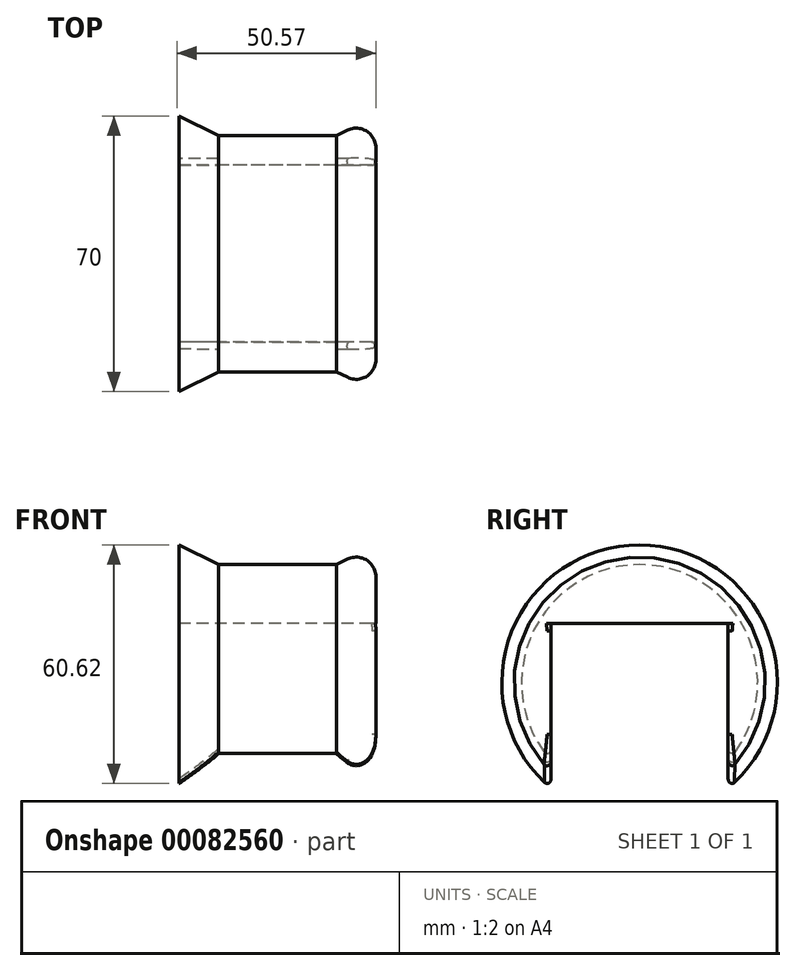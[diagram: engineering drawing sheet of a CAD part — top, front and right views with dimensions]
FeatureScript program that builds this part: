
annotation { "Feature Type Name" : "Feature", "Feature Type Description" : "" }
export const myFeature = defineFeature(function(context is Context, id is Id, definition is map)
    precondition{}
    {
        {
            var Q0;
            Q0=qCreatedBy(makeId("Front.planeOp"),FACE);
            var sketch = newSketch(context, id + "F0", { "sketchPlane" : qUnion([Q0])});
            skLineSegment(sketch, "E0.bottom", {"start": v(0, 0) * mm, "end": v(-50, 0) * mm});
            skLineSegment(sketch, "E0.top", {"start": v(0, 30) * mm, "end": v(-50, 30) * mm});
            skLineSegment(sketch, "E0.left", {"start": v(0, 0) * mm, "end": v(0, 30) * mm});
            skLineSegment(sketch, "E0.right", {"start": v(-50, 0) * mm, "end": v(-50, 30) * mm});
            skLineSegment(sketch, "E1", {"start": v(-50, 30) * mm, "end": v(-50, 35) * mm});
            skLineSegment(sketch, "E2", {"start": v(-50, 35) * mm, "end": v(-40, 30) * mm});
            skLineSegment(sketch, "E3", {"start": v(0, 30) * mm, "end": v(0, 35) * mm});
            skLineSegment(sketch, "E4", {"start": v(0, 35) * mm, "end": v(-10, 30) * mm});
            skSolve(sketch);
        }
        {
            var Q0;
            Q0 = qSketchRegion(id + "F0", true);
            var Q1;
            Q1=sQuery(id+"F0.wireOp",EDGE,"E0.bottom");
            revolve(context, id + "F1", {"entities" : qUnion([Q0]), "axis" : qUnion([Q1]), "revolveType" : RevolveType.FULL});
        }
        {
            var Q0;
            Q0=qCreatedBy(makeId("Top.planeOp"),FACE);
            var sketch = newSketch(context, id + "F2", { "sketchPlane" : qUnion([Q0])});
            skLineSegment(sketch, "E5.bottom", {"start": v(0, 0) * mm, "end": v(-50, 0) * mm, "construction": true});
            skLineSegment(sketch, "E5.top", {"start": v(0, -22.5) * mm, "end": v(-50, -22.5) * mm});
            skLineSegment(sketch, "E5.left", {"start": v(0, 0) * mm, "end": v(0, -22.5) * mm});
            skLineSegment(sketch, "E5.right", {"start": v(-50, 0) * mm, "end": v(-50, -22.5) * mm});
            skLineSegment(sketch, "E6.MirrorCS", {"start": v(-50, 0) * mm, "end": v(-50, 22.5) * mm});
            skLineSegment(sketch, "E7.MirrorCS", {"start": v(0, 22.5) * mm, "end": v(-50, 22.5) * mm});
            skLineSegment(sketch, "E8.MirrorCS", {"start": v(0, 0) * mm, "end": v(0, 22.5) * mm});
            skSolve(sketch);
        }
        {
            var Q0;
            Q0 = qSketchRegion(id + "F2", true);
            extrude(context, id + "F3", {"entities" : qUnion([Q0]), "operationType" : NewBodyOperationType.REMOVE, "endBound" : BoundingType.THROUGH_ALL, "oppositeDirection" : true, "depth" : 25 * mm});
        }
        {
            var Q0;
            Q0 = qSketchRegion(id + "F2", true);
            extrude(context, id + "F4", {"entities" : qUnion([Q0]), "operationType" : NewBodyOperationType.REMOVE, "depth" : 15 * mm});
        }
        {
            var Q0;
            Q0=makeQuery(id+"F1.opRevolve","SWEPT_EDGE",EDGE,{"disambiguationData":[OSD([sQuery(id+"F0.wireOp",EDGE,"E3"),sQuery(id+"F0.wireOp",EDGE,"E4")])]});
            fillet(context, id + "F5", {"entities" : qUnion([Q0]), "radius" : 5 * mm, "tangentPropagation" : true, "allowEdgeOverflow" : false});
        }
        {
            var Q0;
            Q0=makeQuery(id+"F3.boolean.opBoolean","INTERSECT",EDGE,{"derivedFrom":[makeQuery(id+"F1.opRevolve","SWEPT_FACE",FACE,{"disambiguationData":[OSD([sQuery(id+"F0.wireOp",EDGE,"E0.top")])]}),makeQuery(id+"F3.opExtrude","SWEPT_FACE",FACE,{"disambiguationData":[OSD([sQuery(id+"F2.wireOp",EDGE,"E5.top")])]})]});
            var Q1;
            Q1=makeQuery(id+"F3.boolean.opBoolean","INTERSECT",EDGE,{"derivedFrom":[makeQuery(id+"F1.opRevolve","SWEPT_FACE",FACE,{"disambiguationData":[OSD([sQuery(id+"F0.wireOp",EDGE,"E4")])]}),makeQuery(id+"F3.opExtrude","SWEPT_FACE",FACE,{"disambiguationData":[OSD([sQuery(id+"F2.wireOp",EDGE,"E5.top")])]})]});
            var Q2;
            Q2=makeQuery(id+"F3.boolean.opBoolean","INTERSECT",EDGE,{"derivedFrom":[makeQuery(id+"F1.opRevolve","SWEPT_FACE",FACE,{"disambiguationData":[OSD([sQuery(id+"F0.wireOp",EDGE,"E2")])]}),makeQuery(id+"F3.opExtrude","SWEPT_FACE",FACE,{"disambiguationData":[OSD([sQuery(id+"F2.wireOp",EDGE,"E5.top")])]})]});
            var Q3;
            Q3=makeQuery(id+"F3.boolean.opBoolean","INTERSECT",EDGE,{"derivedFrom":[makeQuery(id+"F1.opRevolve","SWEPT_FACE",FACE,{"disambiguationData":[OSD([sQuery(id+"F0.wireOp",EDGE,"E0.top")])]}),makeQuery(id+"F3.opExtrude","SWEPT_FACE",FACE,{"disambiguationData":[OSD([sQuery(id+"F2.wireOp",EDGE,"E7.MirrorCS")])]})]});
            var Q4;
            Q4=makeQuery(id+"F3.boolean.opBoolean","INTERSECT",EDGE,{"derivedFrom":[makeQuery(id+"F1.opRevolve","SWEPT_FACE",FACE,{"disambiguationData":[OSD([sQuery(id+"F0.wireOp",EDGE,"E4")])]}),makeQuery(id+"F3.opExtrude","SWEPT_FACE",FACE,{"disambiguationData":[OSD([sQuery(id+"F2.wireOp",EDGE,"E7.MirrorCS")])]})]});
            var Q5;
            Q5=makeQuery(id+"F3.boolean.opBoolean","INTERSECT",EDGE,{"derivedFrom":[makeQuery(id+"F1.opRevolve","SWEPT_FACE",FACE,{"disambiguationData":[OSD([sQuery(id+"F0.wireOp",EDGE,"E2")])]}),makeQuery(id+"F3.opExtrude","SWEPT_FACE",FACE,{"disambiguationData":[OSD([sQuery(id+"F2.wireOp",EDGE,"E7.MirrorCS")])]})]});
            fillet(context, id + "F6", {"entities" : qUnion([Q0, Q1, Q2, Q3, Q4, Q5]), "radius" : 1 * mm, "tangentPropagation" : true, "allowEdgeOverflow" : false});
        }
    });
